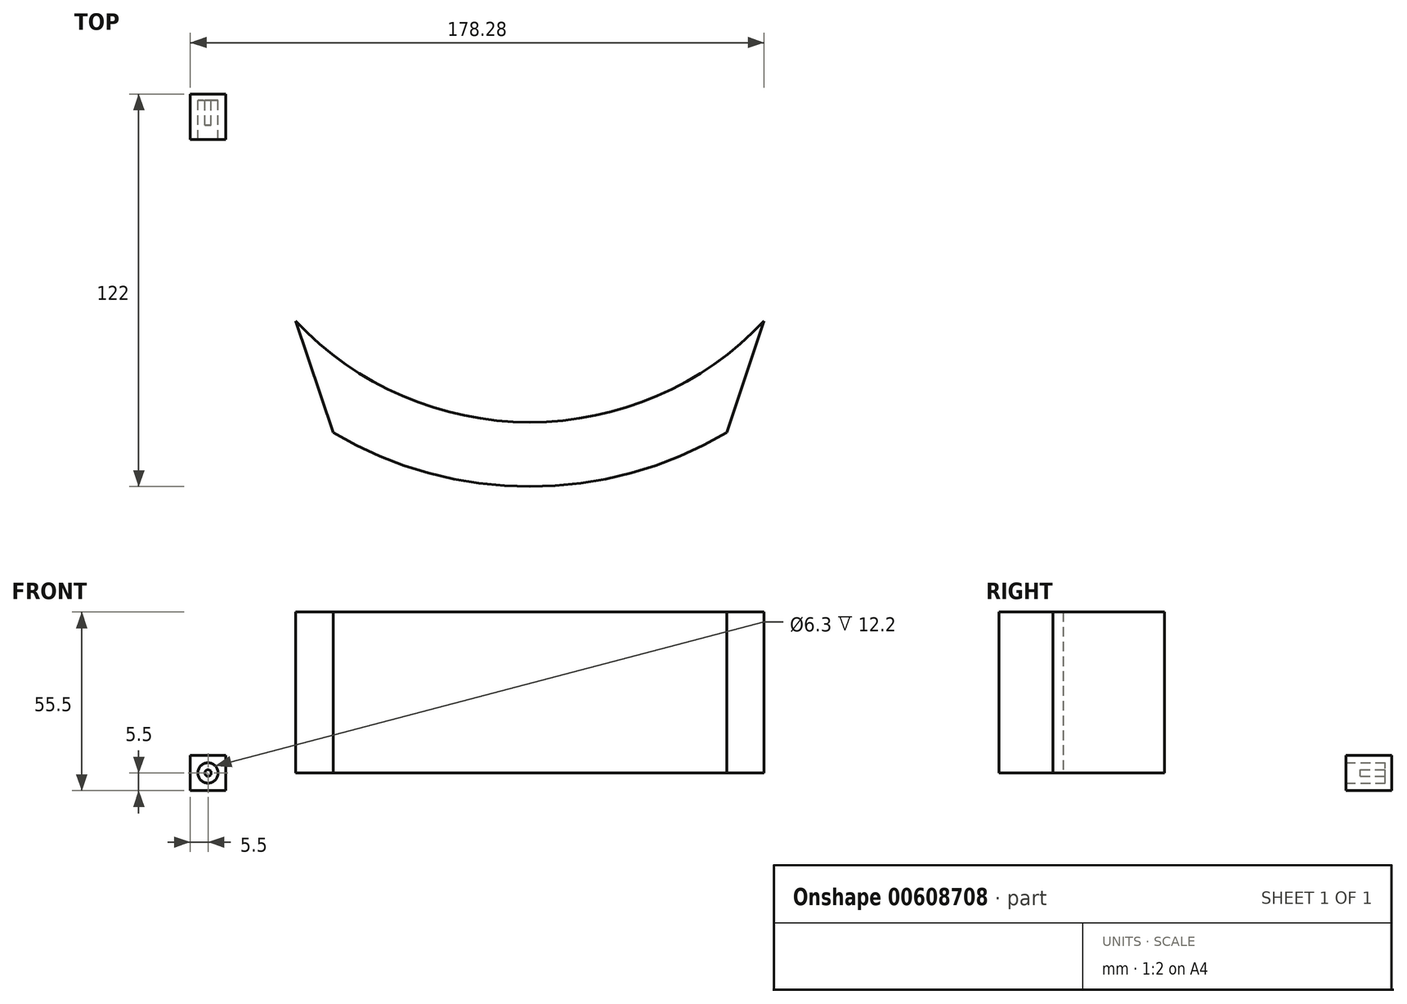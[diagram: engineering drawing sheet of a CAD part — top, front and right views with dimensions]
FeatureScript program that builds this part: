
annotation { "Feature Type Name" : "Feature", "Feature Type Description" : "" }
export const myFeature = defineFeature(function(context is Context, id is Id, definition is map)
    precondition{}
    {
        {
            var Q0;
            Q0=qCreatedBy(makeId("Top.planeOp"),FACE);
            var sketch = newSketch(context, id + "F0", { "sketchPlane" : qUnion([Q0])});
            skArc(sketch, "E0", {"start": v(0, 0) * mm, "mid": v(100, -100) * mm, "end": v(200, 0) * mm});
            skArc(sketch, "E1.0", {"start": v(-20, 0) * mm, "mid": v(100, -120) * mm, "end": v(220, 0) * mm});
            skLineSegment(sketch, "E2", {"start": v(49.83, -86.5) * mm, "end": v(38.85, -103.25) * mm});
            skLineSegment(sketch, "E3", {"start": v(38.85, -103.25) * mm, "end": v(27.22, -68.58) * mm});
            skLineSegment(sketch, "E4", {"start": v(100, 0) * mm, "end": v(100, -100) * mm});
            skLineSegment(sketch, "E5.MirrorCS", {"start": v(150.17, -86.5) * mm, "end": v(161.15, -103.25) * mm});
            skLineSegment(sketch, "E6.MirrorCS", {"start": v(161.15, -103.25) * mm, "end": v(172.78, -68.58) * mm});
            skSolve(sketch);
        }
        {
            var Q0;
            {var subQ0=sQuery(id+"F0.wireOp",EDGE,"E2");Q0=makeQuery(id+"F0.imprint","IMPRINT",FACE,{"disambiguationData":[TD([[makeQuery(id+"F0.imprint","IMPRINT",EDGE,{"derivedFrom":subQ0}),-1.0]])]});}
            var Q1;
            {var subQ0=sQuery(id+"F0.wireOp",EDGE,"E2");Q1=makeQuery(id+"F0.imprint","IMPRINT",FACE,{"disambiguationData":[TD([[makeQuery(id+"F0.imprint","IMPRINT",EDGE,{"derivedFrom":subQ0}),1.0]])]});}
            var Q2;
            {var subQ0=sQuery(id+"F0.wireOp",EDGE,"E5.MirrorCS");Q2=makeQuery(id+"F0.imprint","IMPRINT",FACE,{"disambiguationData":[TD([[makeQuery(id+"F0.imprint","IMPRINT",EDGE,{"derivedFrom":subQ0}),1.0]])]});}
            extrude(context, id + "F1", {"entities" : qUnion([Q0, Q1, Q2]), "depth" : 50 * mm, "offsetDistance" : 25 * mm});
        }
        {
            var Q0;
            Q0=qCreatedBy(makeId("Front.planeOp"),FACE);
            var sketch = newSketch(context, id + "F2", { "sketchPlane" : qUnion([Q0])});
            skLineSegment(sketch, "E7.bottom", {"start": v(5.5, -5.5) * mm, "end": v(-5.5, -5.5) * mm});
            skLineSegment(sketch, "E7.top", {"start": v(5.5, 5.5) * mm, "end": v(-5.5, 5.5) * mm});
            skLineSegment(sketch, "E7.left", {"start": v(5.5, -5.5) * mm, "end": v(5.5, 5.5) * mm});
            skLineSegment(sketch, "E7.right", {"start": v(-5.5, -5.5) * mm, "end": v(-5.5, 5.5) * mm});
            skPoint(sketch, "E7.middle", {"position": v(0, 0) * mm});
            skCircle(sketch, "E8", {"center": v(0, 0) * mm, "radius": 3.15 * mm});
            skSolve(sketch);
        }
        {
            var Q0;
            Q0=makeQuery(id+"F2.imprint","IMPRINT",FACE,{"disambiguationData":[TD([[makeQuery(id+"F2.imprint","IMPRINT",EDGE,{"derivedFrom":sQuery(id+"F2.wireOp",EDGE,"E7.bottom")}),-1.0]])]});
            extrude(context, id + "F3", {"entities" : qUnion([Q0]), "depth" : 12.2 * mm, "offsetDistance" : 25 * mm});
        }
        {
            var Q0;
            Q0=makeQuery(id+"F3.opExtrude","CAP_FACE",FACE,{"disambiguationData":[OSD([sQuery(id+"F2.wireOp",EDGE,"E7.bottom"),sQuery(id+"F2.wireOp",EDGE,"E7.top"),sQuery(id+"F2.wireOp",EDGE,"E7.left"),sQuery(id+"F2.wireOp",EDGE,"E7.right"),sQuery(id+"F2.wireOp",EDGE,"E8")])],"isStart":true});
            var sketch = newSketch(context, id + "F4", { "sketchPlane" : qUnion([Q0])});
            skLineSegment(sketch, "E9.bottom", {"start": v(5.5, -5.5) * mm, "end": v(-5.5, -5.5) * mm});
            skLineSegment(sketch, "E9.top", {"start": v(5.5, 5.5) * mm, "end": v(-5.5, 5.5) * mm});
            skLineSegment(sketch, "E9.left", {"start": v(5.5, -5.5) * mm, "end": v(5.5, 5.5) * mm});
            skLineSegment(sketch, "E9.right", {"start": v(-5.5, -5.5) * mm, "end": v(-5.5, 5.5) * mm});
            skPoint(sketch, "E9.middle", {"position": v(0, 0) * mm});
            skSolve(sketch);
        }
        {
            var Q0;
            Q0 = qSketchRegion(id + "F4", true);
            extrude(context, id + "F5", {"entities" : qUnion([Q0]), "operationType" : NewBodyOperationType.ADD, "depth" : 2 * mm, "offsetDistance" : 25 * mm});
        }
        {
            var Q0;
            Q0=makeQuery(id+"F5.opExtrude","CAP_FACE",FACE,{"disambiguationData":[OSD([sQuery(id+"F4.wireOp",EDGE,"E9.bottom"),sQuery(id+"F4.wireOp",EDGE,"E9.top"),sQuery(id+"F4.wireOp",EDGE,"E9.left"),sQuery(id+"F4.wireOp",EDGE,"E9.right")])],"isStart":true});
            var sketch = newSketch(context, id + "F6", { "sketchPlane" : qUnion([Q0])});
            skCircle(sketch, "E10", {"center": v(0, 0) * mm, "radius": 1 * mm});
            skSolve(sketch);
        }
        {
            var Q0;
            Q0=makeQuery(id+"F6.imprint","IMPRINT",FACE,{"disambiguationData":[TD([[makeQuery(id+"F6.imprint","IMPRINT",EDGE,{"derivedFrom":sQuery(id+"F6.wireOp",EDGE,"E10")}),1.0]])]});
            var Q1;
            Q1=sQuery(id+"F6.wireOp",EDGE,"E10");
            extrude(context, id + "F7", {"entities" : qUnion([Q0]), "surfaceEntities" : qUnion([Q1]), "depth" : 7.7 * mm, "offsetDistance" : 25 * mm});
        }
    });
